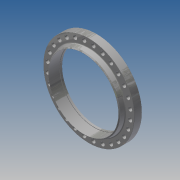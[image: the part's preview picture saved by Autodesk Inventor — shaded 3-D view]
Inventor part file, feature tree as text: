
AUTODESK INVENTOR PART (.ipt)
format: ipt  version: 2017.3 (Build 213257000, 257)  size: 361,984 bytes
history: native  units: in
note: dims shown in document units (in); Inventor stores cm internally (conversion verified against a paired STEP export)
features: sketch x6, extrude x3, chamfer x3, fillet x2, hole x1, pattern_circular x1, plane x1, loft x1, revolve x1, other x1
ambient origin geometry x8: Origin, YZ Plane, XZ Plane, XY Plane, X Axis, Y Axis, Z Axis, Center Point
bodies: Solid1 (feature_tree)
feature tree (20):
  extrude  "Extrusion1"  Depth=3.625in TaperAngle=0.0deg
  hole  "Hole1"  [1 undecoded]
  chamfer  "Chamfer1"  Distance=11.0236in Angle=360.0deg
  pattern_circular  "Circular Pattern1"  [2 undecoded]
  chamfer  "Chamfer2"  Distance=34.0in
  sketch  "Sketch3"  dims[d5=1.875in d6=0.75in d7=0.375in d8=0.25in d9=0.5635in d10=1.0in d11=0.8108in d12=11.0236in d13=360.0deg]
  plane  "Work Plane1"
  extrude  "Extrusion2"  Depth=0.5in TaperAngle=0.0deg
  loft  "Loft1"
  fillet  "Fillet1"  [1 undecoded]
  revolve  "Revolution1"  [1 undecoded]
  extrude  "Extrusion3"  Depth=0.0312in
  fillet  "Fillet3"  Radius=0.5in
  chamfer  "Chamfer4"  Distance=0.4375in
  sketch  "Sketch1"  dims[d0=43.0in d1=3.625in d2=0.0in]
  sketch  "Sketch2"  dims[d3=39.25in d4=0.0442in]
  sketch  "Sketch4"  dims[d15=0.0625in d16=0.125in d17=45.0deg]
  other  "Edges1"
  sketch  "Sketch5"  dims[d18=0.0625in d19=0.125in d20=45.0deg]
  sketch  "Sketch6"  dims[d21=34.75in d22=6.125in d23=34.0in d24=0.5in d25=0.0in d26=0.0in d27=90.0deg d28=0.0in d29=90.0deg d30=0.5in d31=34.0in d32=0.5in d33=0.4375in d37=0.1643in d38=90.0deg d39=32.5in d40=1.0in d41=0.0in d49=0.2577in d50=0.0312in d51=0.0312in d52=0.125in d53=45.0deg]
note: 5 required parameter values undecoded (feature->parameter linkage not recoverable at this tier; creation-order binding heuristic only, values carry confidence <= 0.55)